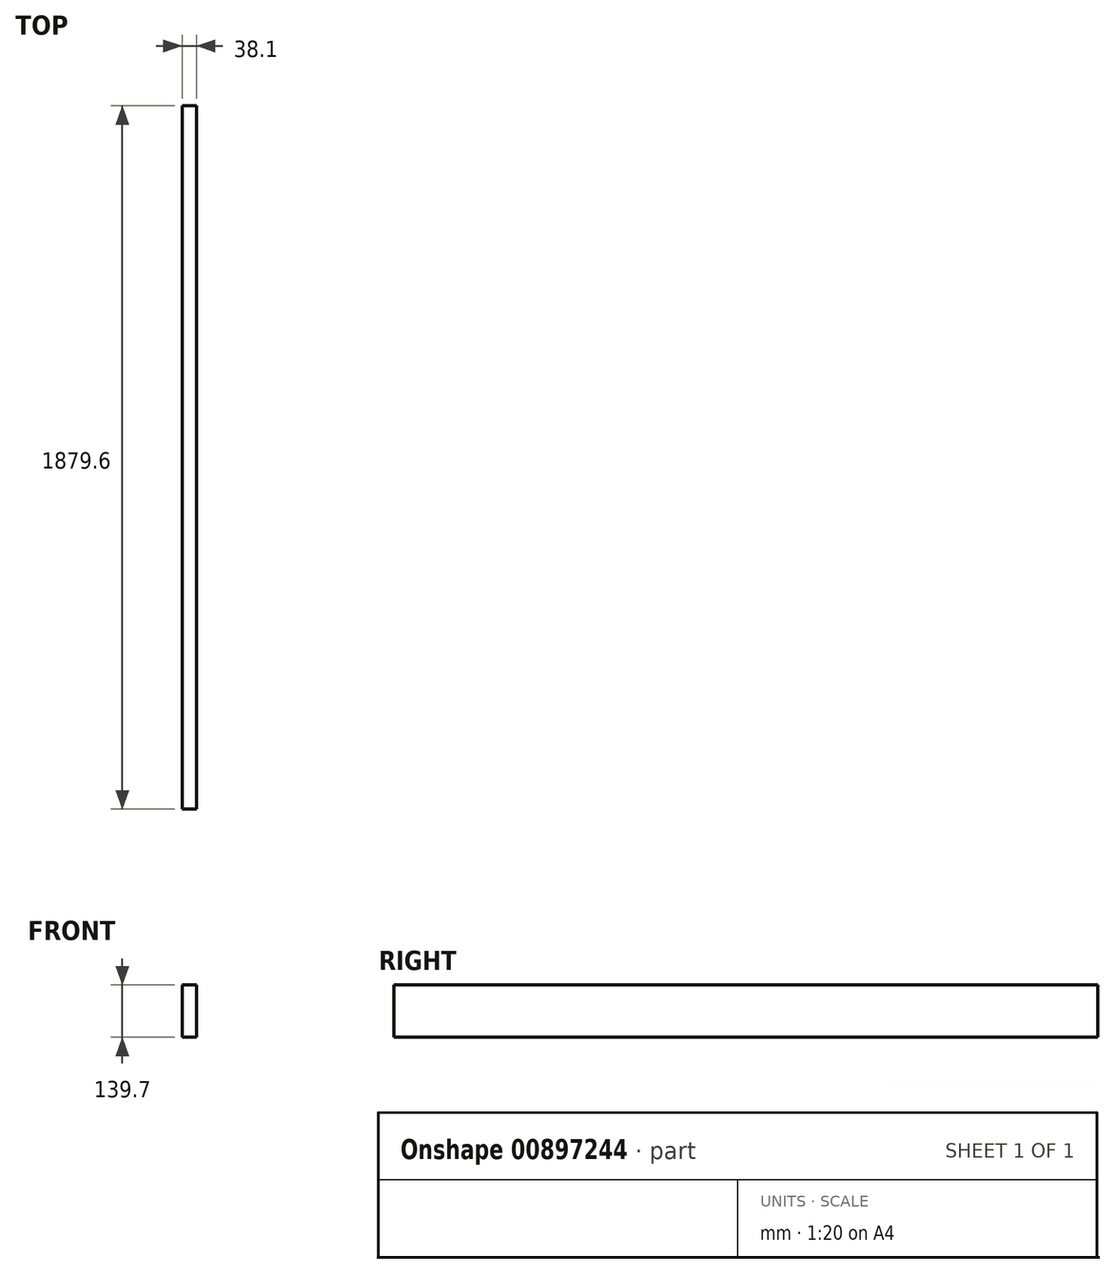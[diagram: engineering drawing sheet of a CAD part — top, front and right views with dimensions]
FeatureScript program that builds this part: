
annotation { "Feature Type Name" : "Feature", "Feature Type Description" : "" }
export const myFeature = defineFeature(function(context is Context, id is Id, definition is map)
    precondition{}
    {
        {
            var Q0;
            Q0=qCreatedBy(makeId("Front.planeOp"),FACE);
            var sketch = newSketch(context, id + "F0", { "sketchPlane" : qUnion([Q0])});
            skLineSegment(sketch, "E0.bottom", {"start": v(-19.05, 69.85) * mm, "end": v(19.05, 69.85) * mm});
            skLineSegment(sketch, "E0.top", {"start": v(-19.05, -69.85) * mm, "end": v(19.05, -69.85) * mm});
            skLineSegment(sketch, "E0.left", {"start": v(-19.05, 69.85) * mm, "end": v(-19.05, -69.85) * mm});
            skLineSegment(sketch, "E0.right", {"start": v(19.05, 69.85) * mm, "end": v(19.05, -69.85) * mm});
            skPoint(sketch, "E0.middle", {"position": v(0, 0) * mm});
            skSolve(sketch);
        }
        {
            var Q0;
            Q0=makeQuery(id+"F0.imprint","IMPRINT",FACE,{"disambiguationData":[TD([[makeQuery(id+"F0.imprint","IMPRINT",EDGE,{"derivedFrom":sQuery(id+"F0.wireOp",EDGE,"E0.bottom")}),-1.0]])]});
            extrude(context, id + "F1", {"entities" : qUnion([Q0]), "depth" : 1879.6 * mm, "offsetDistance" : 25.4 * mm});
        }
    });
